# Revit family: IS_Ceraflex_B1714_BIM_ES
name_source: partatom
category: Plumbing Fixtures
revit_build: Autodesk Revit 2017 (Build: 20160225_1515(x64)
units: mm (PartAtom-declared; Revit-internal decimal feet)

## family parameters
Always vertical = No
Cut with Voids When Loaded = No
OmniClass Number = 23.45.55.17
OmniClass Title = Mixing Faucets
Part Type = Normal
Room Calculation Point = No
Round Connector Dimension = Use Diameter
Shared = No
Work Plane-Based = No

## types (1)
- B1714AA - CERAFLEX BSN MXR RMTD GRANDE 5L/MIN
    Acabado = Cromo
    Accesorios = www.idealstandard.es
    AlturaNominal = 72 mm  [stored 0.23622 ft]
    AnchuraNominal = 185 mm  [stored 0.606955 ft]
    Autor = Ideal Standard s.l.u. (ESP)
    Ayuda = https://www.idealstandard.es
    Cost = 0 $
    CódigoDeBarras = 3800861055891
    DescripciónUniclass2015 = Washbasin taps
    Description = CERAFLEX BSN MXR RMTD GRANDE 5L/MIN
    Destacado = CERAFLEX MONOMANDO LAVABO GRANDE 5L/MIN S/VAL
    Dimensiones = 159 x 144 x 48 mm
    DiámetroDeDesagüe = 0
    Espacio = Interno
    FechaDeCreación = 16/09/2020
    GarantíaDeLasPiezas = 5
    GarantíaPiezas = 5
    GrosorDelMaterial = 0
    GuíaDeInstallación = www.idealstandard.es
    IfcExportaComo = IfcValveType
    InformaciónDeProducto = https://www.idealstandard.es
    Installation instructions = https://www.idealstandard.es
    LongitudNominal = 380 mm
    Maneta = No
    Manufacturer = https://www.idealstandard.es
    Marca = Ideal Standard Iberia
    Model = B1714AA
    NivelDeDesbordamiento = 0
    Nombre = Washbasintaps_Ceraflex_B1714_IdealStandard
    NombreDeObjetoBim = IS_IdealStandard_Washbasintaps_Ceraflex_B1714
    NúmeroDeModelo = B1714AA
    PesoBruto = 0
    PesoNeto = 1.26
    PlatoDeDucha = No
    Product group = Washbasin manual water supply sets
    ProfundidadNominal = 380 mm
    Referencia = B1714
    ReferenciaDeModelo = CERAFLEX MONOMANDO LAVABO GRANDE 5L/MIN S/VAL
    ReferenciaUniclass2015 = Pr_40_20_87_98
    Repuestos = https://www.idealstandard.es
    Revisión = 1
    Teléfono = +34 93 561 80 00
    TestDePresión = 10 bar
    TipoDeConexión = Fontaneria
    TipoDeExportaciónIfc = IfcValveType
    TipoDeGarantía = Garantía del Fabricante
    TipoDeGrifería = Monomando
    URL = https://www.idealstandard.es
    Uniclass 2015 Code = Pr_40_20_87_96
    Uniclass 2015 Name = Washbasin manual water supply sets
    UnidadDeTiempo = año
    UnidadDeVolúmen = Litros
    UnidadDeÁrea = milímetros
    UnidadGarantía = año
    UnidadLineal = milímetros
    UnidadMonetaria = €
    UrlDelFabricante = https://www.idealstandard.es
    Versión = 1
    VersiónUniclass2015 = v1.1

note: [stored X ft] marks values corroborated as IEEE doubles in the binary element streams (Revit-internal decimal feet)

## geometry (parser evidence)
native form markers: Sweep x1
no freeform markers — native parametric forms only
